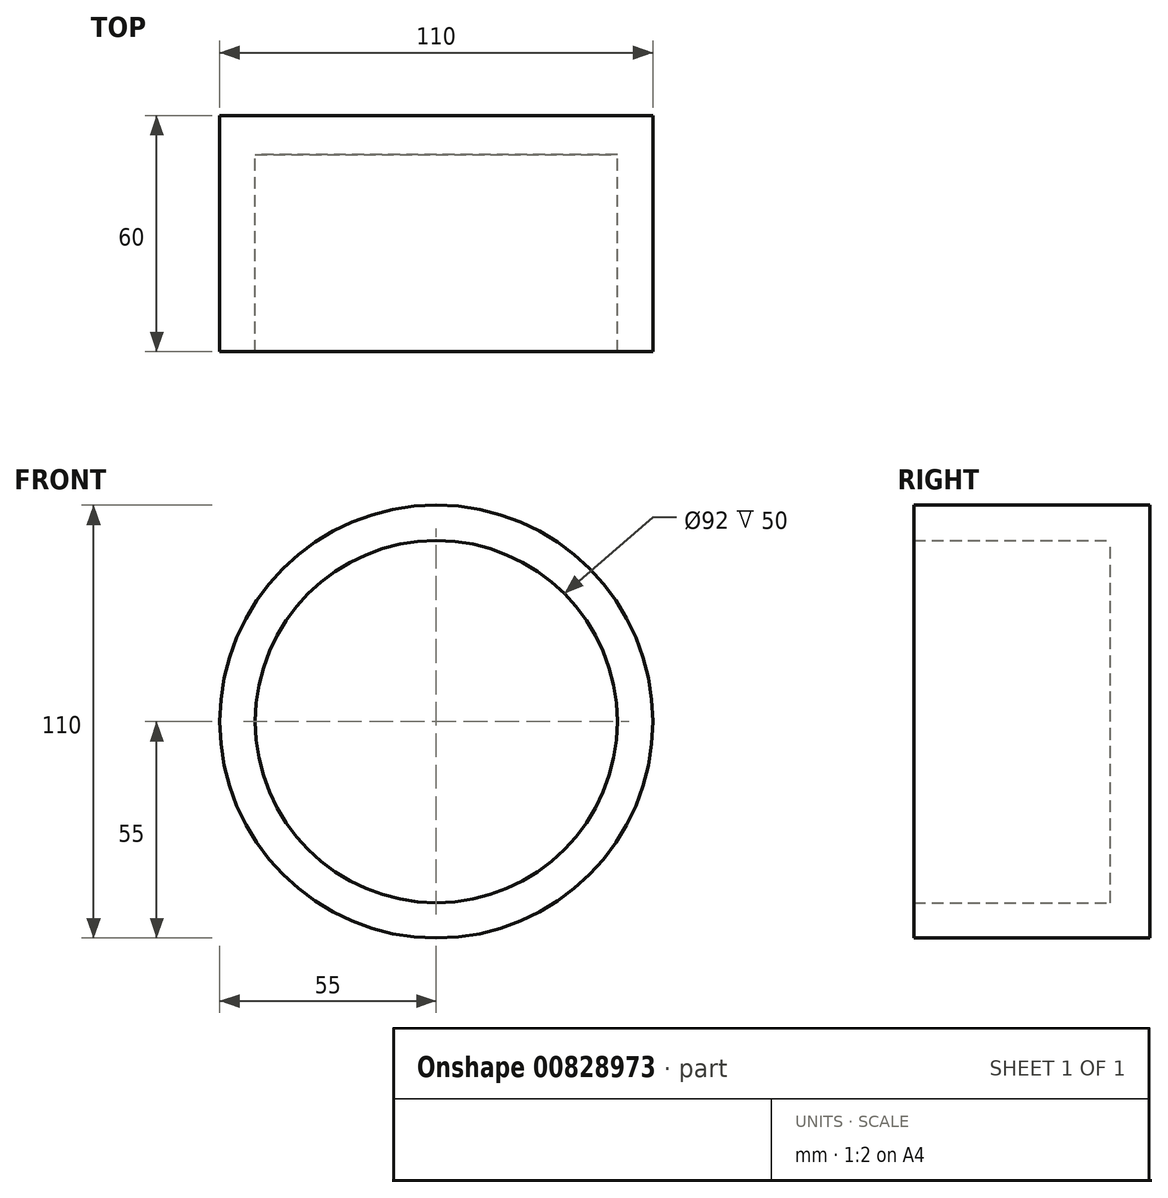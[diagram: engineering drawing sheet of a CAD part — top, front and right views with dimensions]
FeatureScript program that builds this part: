
annotation { "Feature Type Name" : "Feature", "Feature Type Description" : "" }
export const myFeature = defineFeature(function(context is Context, id is Id, definition is map)
    precondition{}
    {
        {
            var Q0;
            Q0=qCreatedBy(makeId("Front.planeOp"),FACE);
            var sketch = newSketch(context, id + "F0", { "sketchPlane" : qUnion([Q0])});
            skCircle(sketch, "E0", {"center": v(0, 0) * mm, "radius": 46 * mm});
            skCircle(sketch, "E1", {"center": v(0, 0) * mm, "radius": 55 * mm});
            skCircle(sketch, "E2", {"center": v(0, 0) * mm, "radius": 45 * mm});
            skSolve(sketch);
        }
        {
            var Q0;
            Q0=makeQuery(id+"F0.imprint","IMPRINT",FACE,{"disambiguationData":[TD([[makeQuery(id+"F0.imprint","IMPRINT",EDGE,{"derivedFrom":sQuery(id+"F0.wireOp",EDGE,"E0")}),-1.0]])]});
            extrude(context, id + "F1", {"entities" : qUnion([Q0]), "depth" : 50 * mm, "offsetDistance" : 25 * mm});
        }
        {
            var Q0;
            Q0=makeQuery(id+"F1.opExtrude","CAP_FACE",FACE,{"disambiguationData":[OSD([sQuery(id+"F0.wireOp",EDGE,"E0"),sQuery(id+"F0.wireOp",EDGE,"E1")])],"isStart":true});
            var sketch = newSketch(context, id + "F2", { "sketchPlane" : qUnion([Q0])});
            skCircle(sketch, "E3", {"center": v(0, 0) * mm, "radius": 55 * mm});
            skSolve(sketch);
        }
        {
            var Q0;
            Q0=qSketchRegion(id+"F2",true);
            extrude(context, id + "F3", {"entities" : qUnion([Q0]), "operationType" : NewBodyOperationType.ADD, "depth" : 10 * mm, "offsetDistance" : 25 * mm});
        }
    });
